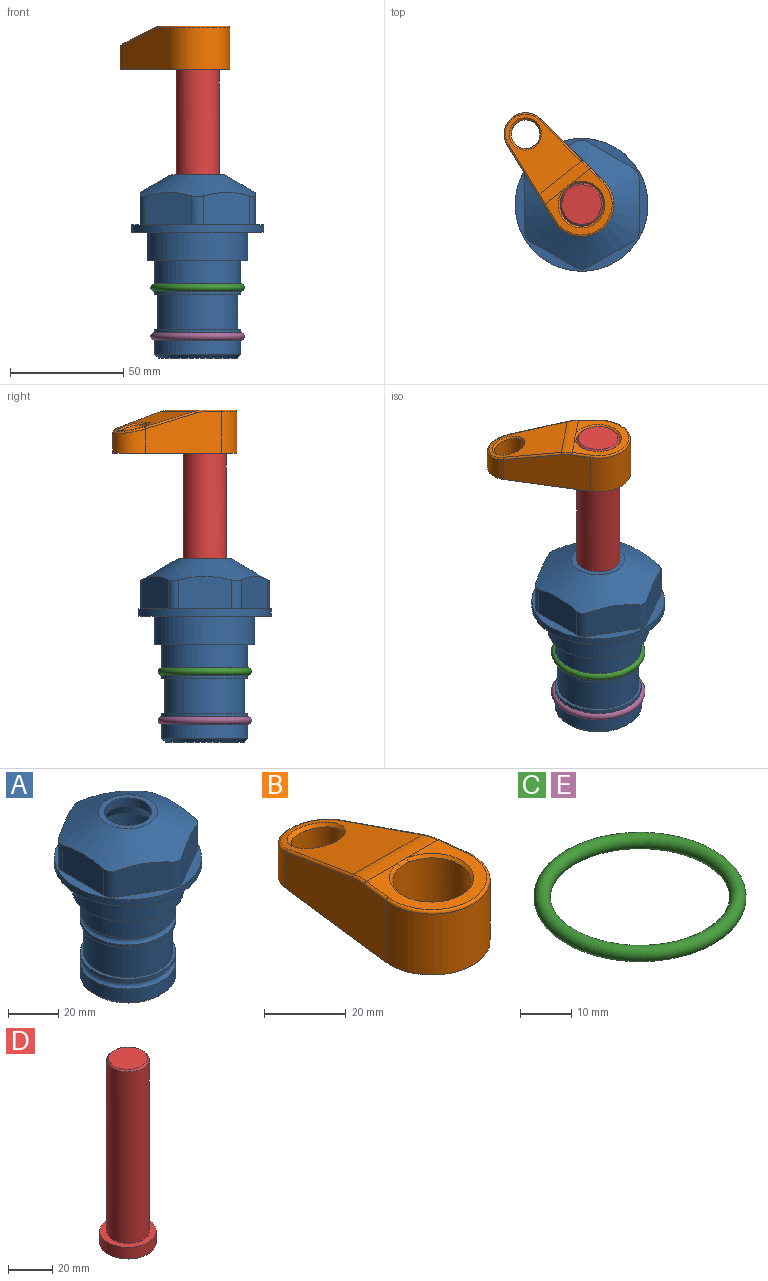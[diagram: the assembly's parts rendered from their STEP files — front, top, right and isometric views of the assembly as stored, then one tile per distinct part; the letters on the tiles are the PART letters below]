
ASSEMBLY  parts=5 mates=4
PART A: 36 faces, bbox 58.7x58.7x81 mm
  f0: cylinder r=17.78mm len=35.56mm, axis (0,0,1), area 1670.8mm2, adj f23,f24,f31
  f1: cylinder r=19.05mm len=38.1mm, axis (0,0,1), area 1191.9mm2, adj f26,f27,f30
  f2: plane 58.66x58.66mm, normal (0,0,-1), area 1150.6mm2, adj f3,f28
  f3: cylinder r=29.33mm len=58.66mm, axis (0,0,-1), area 585.1mm2, adj f2,f4
  f4: plane 58.66x58.66mm, normal (0,0,1), area 475.9mm2, adj f3,f5,f6,f7,f8,f9,f10,f11
  f5: plane 20.32x14.34mm, normal (-0.5,0.87,0), area 324.4mm2, adj f4,f15,f16,f17
  f6: plane 20.32x14.34mm, normal (0.5,0.87,0), area 324.4mm2, adj f4,f14,f15,f17
  f7: plane 23.48x14.34mm, normal (1,0,0), area 324.4mm2, adj f4,f13,f14,f17
  f8: plane 20.32x14.34mm, normal (0.5,-0.87,0), area 324.4mm2, adj f4,f12,f13,f17
  f9: plane 20.32x14.34mm, normal (-0.5,-0.87,0), area 324.4mm2, adj f4,f11,f12,f17
  f10: plane 23.48x14.34mm, normal (-1,0,0), area 324.4mm2, adj f4,f11,f16,f17
  f11: cylinder r=5.08mm len=12.85mm, axis (0,0,-1), area 67.2mm2, adj f4,f9,f10,f17
  f12: cylinder r=5.08mm len=12.85mm, axis (0,0,-1), area 67.2mm2, adj f4,f8,f9,f17
  f13: cylinder r=5.08mm len=12.85mm, axis (0,0,-1), area 67.2mm2, adj f4,f7,f8,f17
  f14: cylinder r=5.08mm len=12.85mm, axis (0,0,-1), area 67.2mm2, adj f4,f6,f7,f17
  f15: cylinder r=5.08mm len=12.85mm, axis (0,0,-1), area 67.2mm2, adj f4,f5,f6,f17
  f16: cylinder r=5.08mm len=12.85mm, axis (0,0,-1), area 67.2mm2, adj f4,f5,f10,f17
  f17: cone r=11.73mm half-angle=60deg, axis (0,0,-1), area 2071.8mm2, adj f5,f6,f7,f8,f9,f10,f11,f12
  f18: plane 23.46x23.46mm, normal (0,0,1), area 147.4mm2, adj f17,f35
  f19: plane 34.93x34.93mm, normal (0,0,-1), area 958mm2, adj f29
  f20: cylinder r=19.05mm len=38.1mm, axis (0,0,1), area 760.1mm2, adj f21,f29
  f21: torus R=19.05mm, axis (0,0,1), area 565.3mm2, adj f20,f22
  f22: cylinder r=19.05mm len=38.1mm, axis (0,0,1), area 190mm2, adj f21,f23
  f23: plane 38.1x38.1mm, normal (0,0,1), area 146.9mm2, adj f0,f22
  f24: plane 38.1x38.1mm, normal (0,0,-1), area 146.9mm2, adj f0,f25
  f25: cylinder r=19.05mm len=38.1mm, axis (0,0,1), area 190mm2, adj f24,f26
  f26: torus R=19.05mm, axis (0,0,1), area 565.3mm2, adj f1,f25
  f27: plane 44.45x44.45mm, normal (0,0,-1), area 411.7mm2, adj f1,f28
  f28: cylinder r=22.23mm len=44.45mm, axis (0,0,1), area 1773.5mm2, adj f2,f27
  f29: cone r=19.05mm half-angle=45deg, axis (0,0,1), area 257.5mm2, adj f19,f20
  f30: cylinder r=3.17mm len=6.75mm, axis (-1,0,0), area 128mm2, adj f1,f33
  f31: cylinder r=3.17mm len=6.35mm, axis (-1,0,0), area 102.5mm2, adj f0,f33
  f32: plane 25.4x25.4mm, normal (0,0,1), area 506.7mm2, adj f33
  f33: cylinder r=12.7mm len=66.42mm, axis (0,0,-1), area 5236.2mm2, adj f30,f31,f32,f34
  f34: cone r=9.53mm half-angle=30deg, axis (0,0,-1), area 443.4mm2, adj f33,f35
  f35: cylinder r=9.53mm len=19.05mm, axis (0,0,-1), area 240.9mm2, adj f18,f34
PART B: 31 faces, bbox 31.7x65.5x19.8 mm
  f0: plane 39.12x18.26mm, normal (0.99,0.12,0), area 612.2mm2, adj f1,f4,f7,f11,f13,f15
  f1: cylinder r=9.53mm len=18.91mm, axis (0,0,-1), area 296.1mm2, adj f0,f2,f7,f17
  f2: plane 39.12x18.26mm, normal (-0.99,0.12,0), area 612.2mm2, adj f1,f4,f7,f12,f14,f16
  f3: cylinder r=6.35mm len=12.7mm, axis (0,0,-1), area 362.4mm2, adj f7,f18
  f4: cylinder r=14.29mm len=28.58mm, axis (0,0,-1), area 882.2mm2, adj f0,f2,f7,f10
  f5: cylinder r=9.53mm len=19.05mm, axis (0,0,-1), area 1092.6mm2, adj f7,f19,f20
  f6: plane 26.99x23.69mm, normal (0,0,1), area 216.2mm2, adj f9,f10,f11,f12,f19
  f7: plane 63.5x28.58mm, normal (0,0,-1), area 661.8mm2, adj f0,f1,f2,f3,f4,f5,f22,f23
  f8: plane 33.52x23.6mm, normal (0,0.26,0.97), area 486mm2, adj f9,f15,f16,f17,f18
  f9: cylinder r=19.05mm len=24.72mm, axis (1,0,0), area 120.4mm2, adj f6,f8,f13,f14,f20
  f10: torus R=13.49mm, axis (0,0,1), area 59mm2, adj f4,f6,f11,f12
  f11: cylinder r=0.79mm len=8.67mm, axis (0.12,-0.99,0), area 10.8mm2, adj f0,f6,f10,f13
  f12: cylinder r=0.79mm len=8.67mm, axis (0.12,0.99,0), area 10.8mm2, adj f2,f6,f10,f14
  f13: bspline ~4.95x1.42mm, area 6.1mm2, adj f0,f9,f11,f15
  f14: bspline ~4.95x1.42mm, area 6.1mm2, adj f2,f9,f12,f16
  f15: cylinder r=0.79mm len=25.95mm, axis (0.12,-0.96,0.26), area 32.9mm2, adj f0,f8,f13,f17
  f16: cylinder r=0.79mm len=25.95mm, axis (0.12,0.96,-0.26), area 32.9mm2, adj f2,f8,f14,f17
  f17: bspline ~18.91x8.38mm, area 30mm2, adj f1,f8,f15,f16
  f18: bspline ~14.29x14.29mm, area 48.3mm2, adj f3,f8
  f19: cone r=9.53mm half-angle=45deg, axis (0,0,1), area 66.5mm2, adj f5,f6,f20
  f20: bspline ~3.22x0.96mm, area 3.5mm2, adj f5,f9,f19
  f21: plane 2.75x2.72mm, normal (0,0,-1), area 2.9mm2, adj f23,f25,f28
  f22: plane 23.05x15.88mm, normal (-0.99,-0.12,0), area 323.6mm2, adj f7,f25,f26,f27,f28,f29
  f23: plane 23.05x15.88mm, normal (0.99,-0.12,0), area 323.6mm2, adj f7,f21,f25,f27,f28,f30
  f24: cylinder r=9.53mm len=10.69mm, axis (0,0,-1), area 114.7mm2, adj f7,f27,f29,f30
  f25: cylinder r=12.7mm len=20.59mm, axis (0,0,-1), area 381.1mm2, adj f7,f21,f22,f23,f26,f28
  f26: plane 2.75x2.72mm, normal (0,0,-1), area 2.9mm2, adj f22,f25,f28
  f27: plane 19.72x18.37mm, normal (0,-0.26,-0.97), area 291.8mm2, adj f22,f23,f24,f28,f29,f30
  f28: cylinder r=15.88mm len=19.92mm, axis (1,0,0), area 54.8mm2, adj f21,f22,f23,f25,f26,f27
  f29: cylinder r=1.59mm len=11mm, axis (0,0,-1), area 34.7mm2, adj f7,f22,f24,f27
  f30: cylinder r=1.59mm len=11mm, axis (0,0,-1), area 34.7mm2, adj f7,f23,f24,f27
PART C: 1 faces, bbox 44.7x44.7x3.2 mm
  f0: torus R=19.05mm, axis (0,0,1), area 1193.9mm2
PART D: 6 faces, bbox 25.4x25.4x101.6 mm
  f0: plane 17.46x17.46mm, normal (0,0,1), area 239.5mm2, adj f5
  f1: plane 25.4x25.4mm, normal (0,0,-1), area 506.7mm2, adj f2
  f2: cylinder r=12.7mm len=25.4mm, axis (0,0,1), area 506.7mm2, adj f1,f3
  f3: plane 25.4x25.4mm, normal (0,0,1), area 221.7mm2, adj f2,f4
  f4: cylinder r=9.53mm len=94.46mm, axis (0,0,1), area 5653mm2, adj f3,f5
  f5: cone r=8.73mm half-angle=45deg, axis (0,0,-1), area 64.4mm2, adj f0,f4
PART E: same geometry as C
PLACE A at identity fixed
PLACE B rot(axis=(0,0,1),38.6deg) t=(0,0,27.55)mm
PLACE C at identity
PLACE D rot(axis=(0,0,1),38.6deg) t=(0,0,27.55)mm
PLACE E t=(0,0,-21.59)mm
MATE cylindrical D.f2 <-> A.f0  axis (0,0,-1) through (0,0,-10.55)mm
MATE fastened A.f0 <-> C.f0  axis (0,0,1) through (0,0,-24.51)mm
MATE fastened A.f0 <-> E.f0  axis (0,0,1) through (0,0,-46.1)mm
MATE fastened D.f2 <-> B.f4  axis (0,0,1) through (0,0,91.05)mm
